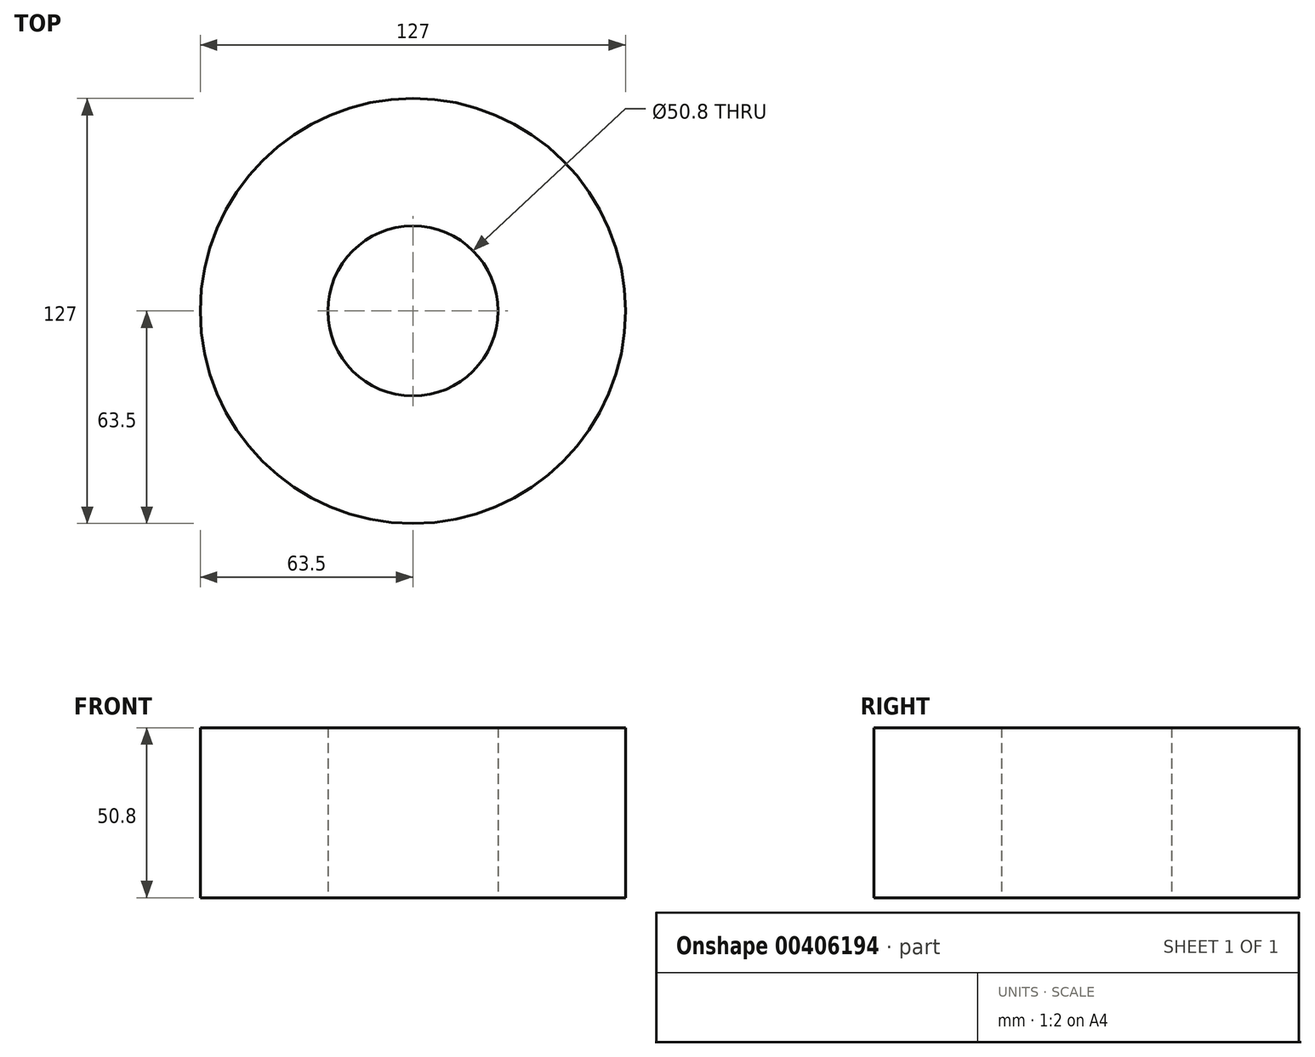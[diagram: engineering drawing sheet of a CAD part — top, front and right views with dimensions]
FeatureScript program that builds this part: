
annotation { "Feature Type Name" : "Feature", "Feature Type Description" : "" }
export const myFeature = defineFeature(function(context is Context, id is Id, definition is map)
    precondition{}
    {
        {
            var Q0;
            Q0=qCreatedBy(makeId("Top.planeOp"),FACE);
            var sketch = newSketch(context, id + "F0", { "sketchPlane" : qUnion([Q0])});
            skCircle(sketch, "E0", {"center": v(0, 0) * mm, "radius": 63.5 * mm});
            skCircle(sketch, "E1", {"center": v(0, 0) * mm, "radius": 25.4 * mm});
            skSolve(sketch);
        }
        {
            var Q0;
            Q0 = qSketchRegion(id + "F0", true);
            extrude(context, id + "F1", {"entities" : qUnion([Q0]), "depth" : 50.8 * mm});
        }
    });
